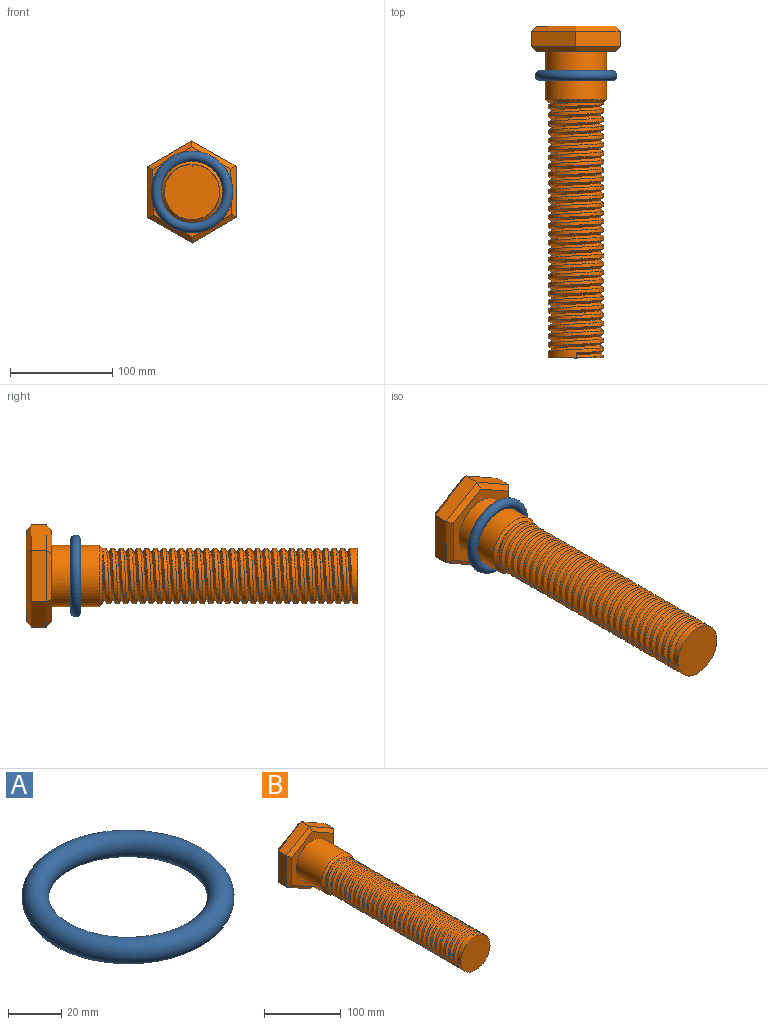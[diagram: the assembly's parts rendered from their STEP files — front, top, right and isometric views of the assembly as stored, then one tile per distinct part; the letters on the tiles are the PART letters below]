
ASSEMBLY  parts=2 mates=1
PART A: 1 faces, bbox 86.6x86.6x10 mm
  f0: torus R=35mm, axis (0,0,1), area 6908.7mm2
PART B: 29 faces, bbox 87x325x100 mm
  f0: cylinder r=27mm len=250mm, axis (0,1,0), area 18468.6mm2, adj f10,f11,f13,f14,f16
  f1: plane 43.12x25.32mm, normal (-0.51,0,0.86), area 750mm2, adj f2,f6,f17,f28
  f2: plane 50x15mm, normal (-1,0,-0.01), area 750mm2, adj f1,f3,f19,f26
  f3: plane 43.48x24.68mm, normal (-0.49,0,-0.87), area 750mm2, adj f2,f4,f21,f24
  f4: plane 43.12x25.32mm, normal (0.51,0,-0.86), area 750mm2, adj f3,f5,f22,f23
  f5: plane 50x15mm, normal (1,0,0.01), area 750mm2, adj f4,f6,f20,f25
  f6: plane 43.48x24.68mm, normal (0.49,0,0.87), area 750mm2, adj f1,f5,f18,f27
  f7: plane 88.45x76.92mm, normal (0,-1,0), area 2254.4mm2, adj f9,f17,f18,f19,f20,f21,f22
  f8: plane 88.45x76.92mm, normal (0,1,0), area 5081.8mm2, adj f23,f24,f25,f26,f27,f28
  f9: cylinder r=30mm len=60mm, axis (0,1,0), area 8859.3mm2, adj f7,f10
  f10: cone r=27mm half-angle=45deg, axis (0,1,0), area 759.7mm2, adj f0,f9,f15
  f11: plane 54x54mm, normal (0,-1,0), area 2290.2mm2, adj f0
  f12: plane 5x4.33mm, normal (-1,0,0), area 10.8mm2, adj f14,f15,f16
  f13: plane 5x4.33mm, normal (1,0,0), area 10.8mm2, adj f0,f14,f16
  f14: bspline ~252.5x54mm, area 23403.7mm2, adj f0,f12,f13,f16
  f15: cylinder r=27mm len=54mm, axis (0,-1,0), area 254.5mm2, adj f10,f12,f16
  f16: bspline ~252.5x54mm, area 23403.7mm2, adj f0,f12,f13,f14,f15
  f17: plane 43.16x28.17mm, normal (-0.36,-0.71,0.61), area 333.1mm2, adj f1,f7,f18,f19
  f18: plane 43.48x27.61mm, normal (0.35,-0.71,0.61), area 333.1mm2, adj f6,f7,f17,f20
  f19: plane 50x5.34mm, normal (-0.71,-0.71,-0.01), area 333.1mm2, adj f2,f7,f17,f21
  f20: plane 50x5.34mm, normal (0.71,-0.71,0.01), area 333.1mm2, adj f5,f7,f18,f22
  f21: plane 43.48x27.61mm, normal (-0.35,-0.71,-0.61), area 333.1mm2, adj f3,f7,f19,f22
  f22: plane 43.16x28.17mm, normal (0.36,-0.71,-0.61), area 333.1mm2, adj f4,f7,f20,f21
  f23: plane 43.16x28.17mm, normal (0.36,0.71,-0.61), area 333.1mm2, adj f4,f8,f24,f25
  f24: plane 43.48x27.61mm, normal (-0.35,0.71,-0.61), area 333.1mm2, adj f3,f8,f23,f26
  f25: plane 50x5.34mm, normal (0.71,0.71,0.01), area 333.1mm2, adj f5,f8,f23,f27
  f26: plane 50x5.34mm, normal (-0.71,0.71,-0.01), area 333.1mm2, adj f2,f8,f24,f28
  f27: plane 43.48x27.61mm, normal (0.35,0.71,0.61), area 333.1mm2, adj f6,f8,f25,f28
  f28: plane 43.16x28.17mm, normal (-0.36,0.71,0.61), area 333.1mm2, adj f1,f8,f26,f27
PLACE A rot(axis=(-1,0,0),90deg) t=(-72.78,31.35,-60.94)mm
PLACE B t=(-72.78,79.85,-60.94)mm
MATE fastened A.f0 <-> B.f0  axis (0,1,0) through (-72.78,31.35,-60.94)mm
